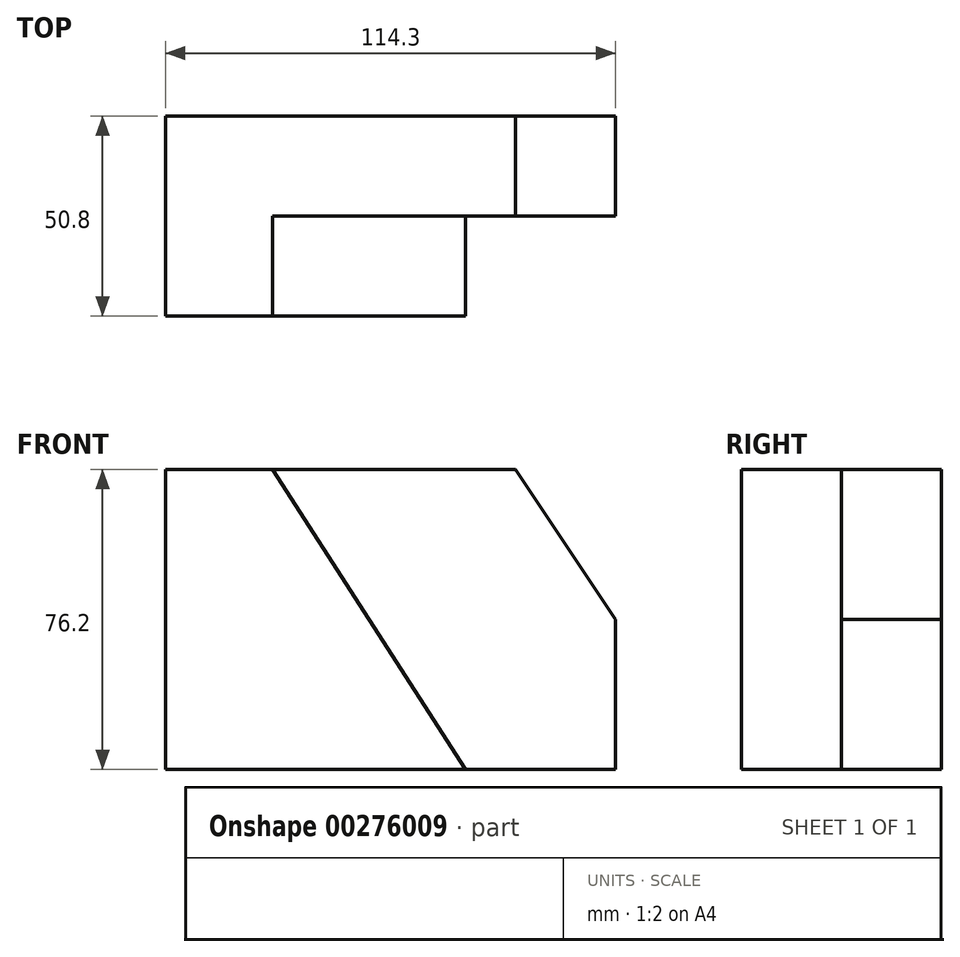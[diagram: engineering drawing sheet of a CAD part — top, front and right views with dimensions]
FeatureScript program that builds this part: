
annotation { "Feature Type Name" : "Feature", "Feature Type Description" : "" }
export const myFeature = defineFeature(function(context is Context, id is Id, definition is map)
    precondition{}
    {
        {
            var Q0;
            Q0=qCreatedBy(makeId("Front.planeOp"),FACE);
            var sketch = newSketch(context, id + "F0", { "sketchPlane" : qUnion([Q0])});
            skLineSegment(sketch, "E0.bottom", {"start": v(0, 0) * mm, "end": v(114.3, 0) * mm});
            skLineSegment(sketch, "E0.top", {"start": v(0, 76.2) * mm, "end": v(88.9, 76.2) * mm});
            skLineSegment(sketch, "E0.left", {"start": v(0, 0) * mm, "end": v(0, 76.2) * mm});
            skLineSegment(sketch, "E0.right", {"start": v(114.3, 0) * mm, "end": v(114.3, 38.1) * mm});
            skLineSegment(sketch, "E1", {"start": v(88.9, 76.2) * mm, "end": v(114.3, 38.1) * mm});
            skSolve(sketch);
        }
        {
            var Q0;
            Q0 = qSketchRegion(id + "F0", true);
            extrude(context, id + "F1", {"entities" : qUnion([Q0]), "depth" : 25.4 * mm});
        }
        {
            var Q0;
            Q0=makeQuery(id+"F1.opExtrude","CAP_FACE",FACE,{"disambiguationData":[OSD([sQuery(id+"F0.wireOp",EDGE,"E0.bottom"),sQuery(id+"F0.wireOp",EDGE,"E0.top"),sQuery(id+"F0.wireOp",EDGE,"E0.left"),sQuery(id+"F0.wireOp",EDGE,"E0.right"),sQuery(id+"F0.wireOp",EDGE,"E1")])],"isStart":false});
            var sketch = newSketch(context, id + "F2", { "sketchPlane" : qUnion([Q0])});
            skLineSegment(sketch, "E2", {"start": v(1.75, 76.2) * mm, "end": v(27.15, 76.2) * mm});
            skLineSegment(sketch, "E3", {"start": v(0, 76.2) * mm, "end": v(0, 0) * mm});
            skLineSegment(sketch, "E4", {"start": v(27.15, 76.2) * mm, "end": v(76.2, 0) * mm});
            skLineSegment(sketch, "E5", {"start": v(0, 0) * mm, "end": v(76.2, 0) * mm});
            skSolve(sketch);
        }
        {
            var Q0;
            Q0 = qSketchRegion(id + "F2", true);
            var Q1;
            {var subQ1=sQuery(id+"F2.wireOp",EDGE,"E2");Q1=makeQuery(id+"F2.imprint","IMPRINT",FACE,{"disambiguationData":[TD([[makeQuery(id+"F2.imprint","IMPRINT",EDGE,{"derivedFrom":subQ1}),-1.0]])]});}
            extrude(context, id + "F3", {"entities" : qUnion([Q0, Q1]), "operationType" : NewBodyOperationType.ADD, "depth" : 25.4 * mm});
        }
    });
